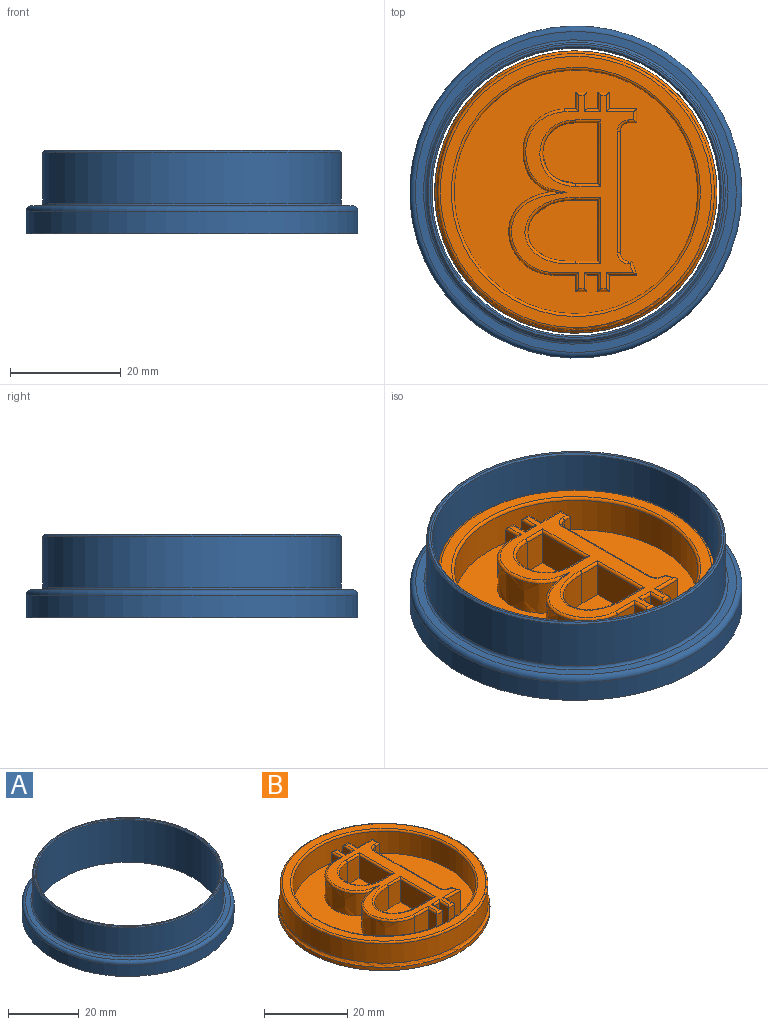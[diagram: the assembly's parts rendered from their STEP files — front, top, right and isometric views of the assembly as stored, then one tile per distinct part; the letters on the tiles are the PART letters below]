
ASSEMBLY  parts=2 mates=1
PART A: 10 faces, bbox 64.9x64.9x15 mm
  f0: cylinder r=26mm len=52mm, axis (0,0,-1), area 2401.4mm2, adj f3,f7
  f1: cylinder r=27mm len=54mm, axis (0,0,-1), area 1560.7mm2, adj f6,f8
  f2: plane 53.4x53.4mm, normal (0,0,1), area 66.6mm2, adj f6,f7
  f3: plane 60x60mm, normal (0,0,-1), area 703.7mm2, adj f0,f4
  f4: cylinder r=30mm len=60mm, axis (0,0,-1), area 754mm2, adj f3,f9
  f5: plane 58x58mm, normal (0,0,1), area 266.2mm2, adj f8,f9
  f6: cone r=26.7mm half-angle=45deg, axis (0,0,-1), area 71.6mm2, adj f1,f2
  f7: cone r=26mm half-angle=45deg, axis (0,0,1), area 69.7mm2, adj f0,f2
  f8: torus R=27.5mm, axis (0,0,1), area 134.1mm2, adj f1,f5
  f9: torus R=29mm, axis (0,0,1), area 292.5mm2, adj f4,f5
PART B: 82 faces, bbox 56.3x56.3x8 mm
  f0: plane 44x44mm, normal (0,0,1), area 964.6mm2, adj f4,f12,f13,f14,f15,f16,f17,f18
  f1: cylinder r=25.5mm len=51mm, axis (0,0,-1), area 160.2mm2, adj f2,f81
  f2: plane 51x51mm, normal (0,0,-1), area 2042.8mm2, adj f1
  f3: cylinder r=25mm len=50mm, axis (0,0,-1), area 885mm2, adj f44,f81
  f4: cylinder r=22mm len=44mm, axis (0,0,-1), area 898.5mm2, adj f0,f45
  f5: plane 49x49mm, normal (0,0,1), area 295.3mm2, adj f44,f45
  f6: extruded ~11x6.5mm, area 118.6mm2, adj f7,f40,f43,f80
  f7: plane 6.5x4mm, normal (0,-1,0), area 26mm2, adj f6,f8,f43,f78
  f8: plane 11x6.5mm, normal (-1,0,0), area 71.5mm2, adj f7,f40,f43,f77
  f9: extruded ~11.03x8.7mm, area 149.3mm2, adj f10,f38,f42,f76
  f10: plane 6.5x4mm, normal (0,-1,0), area 26mm2, adj f9,f11,f42,f74
  f11: plane 11x6.5mm, normal (-1,0,0), area 71.5mm2, adj f10,f38,f42,f73
  f12: plane 6.5x3mm, normal (1,0,0), area 19.5mm2, adj f0,f13,f39,f46
  f13: plane 6.5x2mm, normal (0,1,0), area 13mm2, adj f0,f12,f14,f47
  f14: plane 6.5x3mm, normal (-1,0,0), area 19.5mm2, adj f0,f13,f15,f49
  f15: plane 6.5x2mm, normal (0,1,0), area 13mm2, adj f0,f14,f16,f51
  f16: extruded ~15x7.55mm, area 140.1mm2, adj f0,f15,f17,f53
  f17: extruded ~15x7.63mm, area 153mm2, adj f0,f16,f18,f55
  f18: plane 6.5x4.5mm, normal (0,-1,0), area 29.3mm2, adj f0,f17,f19,f57
  f19: plane 6.5x3mm, normal (-1,0,0), area 19.5mm2, adj f0,f18,f20,f59
  f20: plane 6.5x2mm, normal (0,-1,0), area 13mm2, adj f0,f19,f21,f61
  f21: plane 6.5x3mm, normal (1,0,0), area 19.5mm2, adj f0,f20,f22,f63
  f22: plane 6.5x2mm, normal (0,-1,0), area 13mm2, adj f0,f21,f23,f65
  f23: plane 6.5x3mm, normal (-1,0,0), area 19.5mm2, adj f0,f22,f24,f67
  f24: plane 6.5x2mm, normal (0,-1,0), area 13mm2, adj f0,f23,f25,f69
  f25: plane 6.5x3mm, normal (1,0,0), area 19.5mm2, adj f0,f24,f26,f71
  f26: plane 6.5x5mm, normal (0,-1,0), area 32.5mm2, adj f0,f25,f27,f72
  f27: plane 6.5x2.5mm, normal (0.94,0.34,0), area 17.3mm2, adj f0,f26,f28,f70
  f28: plane 6.5x0.59mm, normal (0,1,0), area 3.8mm2, adj f0,f27,f29,f68
  f29: cylinder r=1.5mm len=6.5mm, axis (0,0,-1), area 15.3mm2, adj f0,f28,f30,f66
  f30: plane 22x6.5mm, normal (1,0,0), area 143mm2, adj f0,f29,f31,f64
  f31: cylinder r=1.5mm len=6.5mm, axis (0,0,-1), area 15.3mm2, adj f0,f30,f32,f62
  f32: plane 6.5x1.5mm, normal (0,-1,0), area 9.7mm2, adj f0,f31,f33,f60
  f33: plane 6.5x2.5mm, normal (1,0,0), area 16.2mm2, adj f0,f32,f34,f58
  f34: plane 6.5x5mm, normal (0,1,0), area 32.5mm2, adj f0,f33,f35,f56
  f35: plane 6.5x3mm, normal (1,0,0), area 19.5mm2, adj f0,f34,f36,f54
  f36: plane 6.5x2mm, normal (0,1,0), area 13mm2, adj f0,f35,f37,f52
  f37: plane 6.5x3mm, normal (-1,0,0), area 19.5mm2, adj f0,f36,f39,f50
  f38: plane 6.5x4mm, normal (0,1,0), area 26mm2, adj f9,f11,f42,f75
  f39: plane 6.5x2mm, normal (0,1,0), area 13mm2, adj f0,f12,f37,f48
  f40: plane 6.5x4mm, normal (0,1,0), area 26mm2, adj f6,f8,f43,f79
  f41: plane 35x22.14mm, normal (0,0,1), area 229.9mm2, adj f46,f47,f48,f49,f50,f51,f52,f53
  f42: plane 14.57x11.89mm, normal (0,0,1), area 122.1mm2, adj f9,f10,f11,f38
  f43: plane 11.36x11mm, normal (0,0,1), area 96.8mm2, adj f6,f7,f8,f40
  f44: torus R=24.5mm, axis (0,0,1), area 122.5mm2, adj f3,f5
  f45: torus R=22.5mm, axis (0,0,1), area 109.5mm2, adj f4,f5
  f46: cylinder r=0.5mm len=3.5mm, axis (0,-1,0), area 2.4mm2, adj f12,f41,f47,f48
  f47: cylinder r=0.5mm len=2mm, axis (1,0,0), area 1.2mm2, adj f13,f41,f46,f49
  f48: cylinder r=0.5mm len=3mm, axis (1,0,0), area 2mm2, adj f39,f41,f46,f50
  f49: cylinder r=0.5mm len=3.5mm, axis (0,1,0), area 2.4mm2, adj f14,f41,f47,f51
  f50: cylinder r=0.5mm len=3.5mm, axis (0,1,0), area 2.4mm2, adj f37,f41,f48,f52
  f51: cylinder r=0.5mm len=2.5mm, axis (1,0,0), area 1.8mm2, adj f15,f41,f49,f53
  f52: cylinder r=0.5mm len=2mm, axis (1,0,0), area 1.2mm2, adj f36,f41,f50,f54
  f53: bspline ~16.16x10.52mm, area 17.6mm2, adj f16,f41,f51,f55
  f54: cylinder r=0.5mm len=3.5mm, axis (0,-1,0), area 2.4mm2, adj f35,f41,f52,f56
  f55: bspline ~15.72x12.45mm, area 19.1mm2, adj f17,f41,f53,f57
  f56: cylinder r=0.5mm len=5.5mm, axis (1,0,0), area 3.9mm2, adj f34,f41,f54,f58
  f57: cylinder r=0.5mm len=5mm, axis (-1,0,0), area 3.7mm2, adj f18,f41,f55,f59
  f58: cylinder r=0.5mm len=2.5mm, axis (0,-1,0), area 1.6mm2, adj f33,f41,f56,f60
  f59: cylinder r=0.5mm len=3.5mm, axis (0,1,0), area 2.4mm2, adj f19,f41,f57,f61
  f60: cylinder r=0.5mm len=1.5mm, axis (-1,0,0), area 1mm2, adj f32,f41,f58,f62
  f61: cylinder r=0.5mm len=2mm, axis (-1,0,0), area 1.2mm2, adj f20,f41,f59,f63
  f62: torus R=2mm, axis (0,0,1), area 2.1mm2, adj f31,f41,f60,f64
  f63: cylinder r=0.5mm len=3.5mm, axis (0,-1,0), area 2.4mm2, adj f21,f41,f61,f65
  f64: cylinder r=0.5mm len=22mm, axis (0,-1,0), area 17.3mm2, adj f30,f41,f62,f66
  f65: cylinder r=0.5mm len=3mm, axis (-1,0,0), area 2mm2, adj f22,f41,f63,f67
  f66: torus R=2mm, axis (0,0,1), area 2.1mm2, adj f29,f41,f64,f68
  f67: cylinder r=0.5mm len=3.5mm, axis (0,1,0), area 2.4mm2, adj f23,f41,f65,f69
  f68: cylinder r=0.5mm len=0.59mm, axis (1,0,0), area 0.3mm2, adj f28,f41,f66,f70
  f69: cylinder r=0.5mm len=2mm, axis (-1,0,0), area 1.2mm2, adj f24,f41,f67,f71
  f70: cylinder r=0.5mm len=2.67mm, axis (0.34,-0.94,0), area 1.7mm2, adj f27,f41,f68,f72
  f71: cylinder r=0.5mm len=3.5mm, axis (0,-1,0), area 2.4mm2, adj f25,f41,f69,f72
  f72: cylinder r=0.5mm len=5.5mm, axis (-1,0,0), area 3.8mm2, adj f26,f41,f70,f71
  f73: cylinder r=0.5mm len=12mm, axis (0,1,0), area 9mm2, adj f11,f41,f74,f75
  f74: cylinder r=0.5mm len=4.5mm, axis (-1,0,0), area 3.3mm2, adj f10,f41,f73,f76
  f75: cylinder r=0.5mm len=4.5mm, axis (1,0,0), area 3.3mm2, adj f38,f41,f73,f76
  f76: bspline ~12.03x9.85mm, area 18.5mm2, adj f9,f41,f74,f75
  f77: cylinder r=0.5mm len=12mm, axis (0,1,0), area 9mm2, adj f8,f41,f78,f79
  f78: cylinder r=0.5mm len=4.5mm, axis (-1,0,0), area 3.3mm2, adj f7,f41,f77,f80
  f79: cylinder r=0.5mm len=4.5mm, axis (1,0,0), area 3.3mm2, adj f40,f41,f77,f80
  f80: bspline ~13.4x12mm, area 14.8mm2, adj f6,f41,f78,f79
  f81: torus R=26mm, axis (0,0,-1), area 165.6mm2, adj f1,f3
PLACE A at identity
PLACE B at identity
MATE fastened B.f1 <-> A.f4  axis (0,0,-1) through (0,0,0)mm
